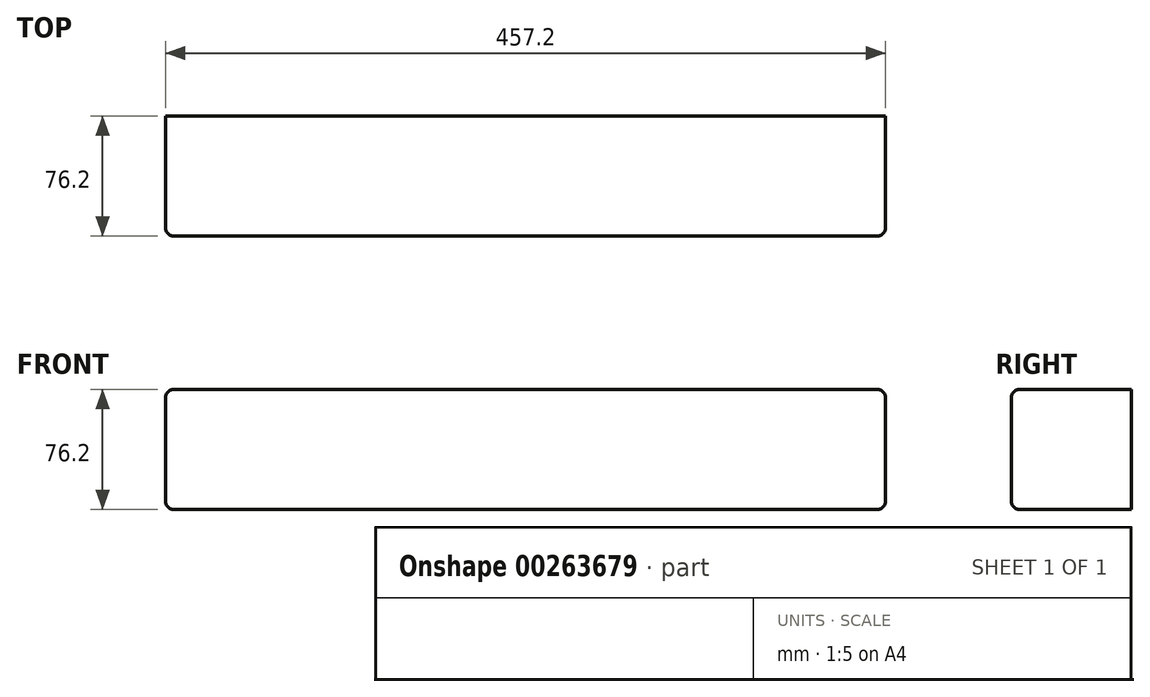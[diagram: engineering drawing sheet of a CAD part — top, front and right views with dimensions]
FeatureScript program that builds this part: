
annotation { "Feature Type Name" : "Feature", "Feature Type Description" : "" }
export const myFeature = defineFeature(function(context is Context, id is Id, definition is map)
    precondition{}
    {
        {
            var Q0;
            Q0=qCreatedBy(makeId("Front.planeOp"),FACE);
            var sketch = newSketch(context, id + "F0", { "sketchPlane" : qUnion([Q0])});
            skLineSegment(sketch, "E0.bottom", {"start": v(0, 76.2) * mm, "end": v(457.2, 76.2) * mm});
            skLineSegment(sketch, "E0.top", {"start": v(0, 0) * mm, "end": v(457.2, 0) * mm});
            skLineSegment(sketch, "E0.left", {"start": v(0, 76.2) * mm, "end": v(0, 0) * mm});
            skLineSegment(sketch, "E0.right", {"start": v(457.2, 76.2) * mm, "end": v(457.2, 0) * mm});
            skLineSegment(sketch, "E1", {"start": v(406.4, 76.2) * mm, "end": v(406.4, 0) * mm});
            skLineSegment(sketch, "E2", {"start": v(50.8, 76.2) * mm, "end": v(50.8, 0) * mm});
            skSolve(sketch);
        }
        {
            var Q0;
            Q0 = qSketchRegion(id + "F0", true);
            extrude(context, id + "F1", {"entities" : qUnion([Q0]), "depth" : 76.2 * mm});
        }
        {
            var Q0;
            Q0=makeQuery(id+"F1.opExtrude","SWEPT_EDGE",EDGE,{"disambiguationData":[OSD([sQuery(id+"F0.wireOp",EDGE,"E0.top"),sQuery(id+"F0.wireOp",EDGE,"E0.right")])]});
            var Q1;
            Q1=makeQuery(id+"F1.opExtrude","SWEPT_EDGE",EDGE,{"disambiguationData":[OSD([sQuery(id+"F0.wireOp",EDGE,"E0.top"),sQuery(id+"F0.wireOp",EDGE,"E0.left")])]});
            var Q2;
            Q2=makeQuery(id+"F1.opExtrude","SWEPT_EDGE",EDGE,{"disambiguationData":[OSD([sQuery(id+"F0.wireOp",EDGE,"E0.bottom"),sQuery(id+"F0.wireOp",EDGE,"E0.right")])]});
            var Q3;
            Q3=makeQuery(id+"F1.opExtrude","SWEPT_EDGE",EDGE,{"disambiguationData":[OSD([sQuery(id+"F0.wireOp",EDGE,"E0.bottom"),sQuery(id+"F0.wireOp",EDGE,"E0.left")])]});
            fillet(context, id + "F2", {"entities" : qUnion([Q0, Q1, Q2, Q3]), "radius" : 5.08 * mm, "tangentPropagation" : true, "allowEdgeOverflow" : false});
        }
        {
            var Q0;
            Q0=makeQuery(id+"F1.opExtrude","CAP_EDGE",EDGE,{"disambiguationData":[OSD([sQuery(id+"F0.wireOp",EDGE,"E0.bottom")])],"isStart":false});
            fillet(context, id + "F3", {"entities" : qUnion([Q0]), "radius" : 5.08 * mm, "tangentPropagation" : true, "allowEdgeOverflow" : false});
        }
    });
